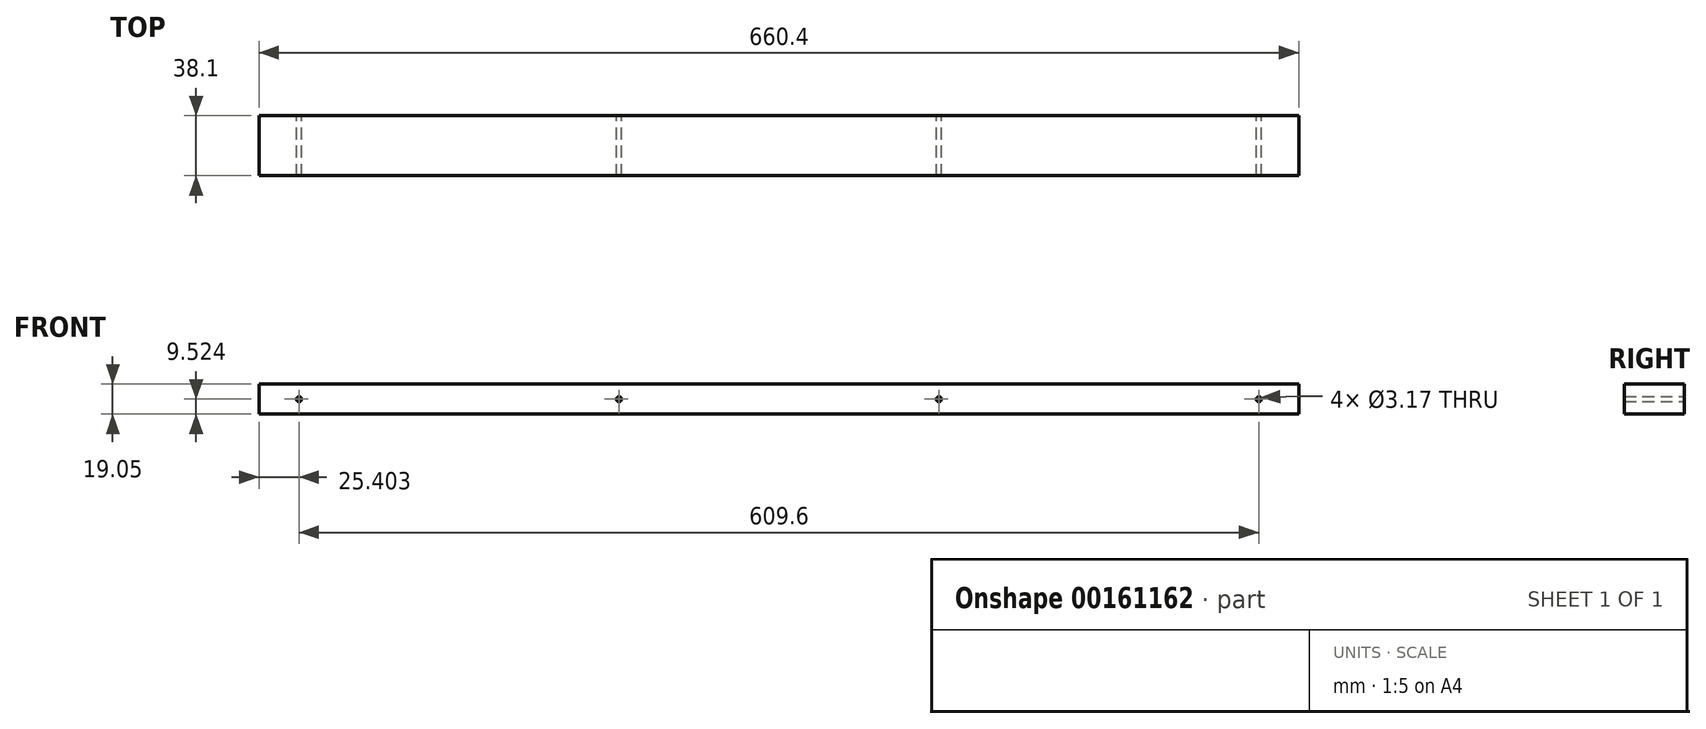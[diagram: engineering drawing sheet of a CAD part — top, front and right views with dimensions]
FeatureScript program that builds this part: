
annotation { "Feature Type Name" : "Feature", "Feature Type Description" : "" }
export const myFeature = defineFeature(function(context is Context, id is Id, definition is map)
    precondition{}
    {
        {
            var Q0;
            Q0=qCreatedBy(makeId("Front.planeOp"),FACE);
            var sketch = newSketch(context, id + "F0", { "sketchPlane" : qUnion([Q0])});
            skLineSegment(sketch, "E0.bottom", {"start": v(-294.46, 64.02) * mm, "end": v(365.94, 64.02) * mm});
            skLineSegment(sketch, "E0.top", {"start": v(-294.46, 44.97) * mm, "end": v(365.94, 44.97) * mm});
            skLineSegment(sketch, "E0.left", {"start": v(-294.46, 64.02) * mm, "end": v(-294.46, 44.97) * mm});
            skLineSegment(sketch, "E0.right", {"start": v(365.94, 64.02) * mm, "end": v(365.94, 44.97) * mm});
            skCircle(sketch, "E1", {"center": v(-269.06, 54.5) * mm, "radius": 1.59 * mm});
            skCircle(sketch, "E2", {"center": v(-65.86, 54.5) * mm, "radius": 1.59 * mm});
            skCircle(sketch, "E3", {"center": v(137.34, 54.5) * mm, "radius": 1.59 * mm});
            skCircle(sketch, "E4", {"center": v(340.54, 54.5) * mm, "radius": 1.59 * mm});
            skSolve(sketch);
        }
        {
            var Q0;
            Q0=makeQuery(id+"F0.imprint","IMPRINT",FACE,{"disambiguationData":[TD([[makeQuery(id+"F0.imprint","IMPRINT",EDGE,{"derivedFrom":sQuery(id+"F0.wireOp",EDGE,"E0.bottom")}),-1.0]])]});
            extrude(context, id + "F1", {"entities" : qUnion([Q0]), "depth" : 38.1 * mm});
        }
    });
